# Revit family: bespoke
name_source: partatom
category: Furniture
revit_build: Autodesk Revit 2015 (Build: 20140903_1530(x64)
units: mm (PartAtom-declared; Revit-internal decimal feet)

## types (12) — shared parameters
BIMobject category = Tables
BOSUseNativeGeometries = 1
Brand url = http://www.swedese.com
Date of publishing = 3/22/2016
Design country = Sweden
Edition number = 1
IFC Classification = Furnishing Element
Manufacturer country = Sweden
Manufacturer name = Swedese
Material main = Wood
Nominal height = 720
Nominal width = 2000
OmniClass Code = 23-21 11 00
OmniClass Description = Commercial Furniture
Product Guid = 040cca99-c903-4709-9778-d5a774ea8faa
Product SKU = 27924
Product data url = https://bimobject.com
Product family = Tables
Product group = Bespoke
Product name = Bespoke
Product url = http://www.swedese.se
QR code = http://bimobject.com
Technical description = https://static-swedese.s3.amazonaws.com
UNSPSC Code = 56
Uniclass 1.4 Code = L8211
Uniclass 1.4 Description = Furniture
Weight Net (Kg) = 55

## type names (no varying parameters)
- TYPE - (Bespoke Addon Right) COLOUR - (Ash veneer)
- TYPE - (Bespoke Addon Left) COLOUR - (Ash veneer)
- TYPE - (Bespoke Addon Both) COLOUR - (Ash veneer)
- TYPE - (Bespoke 1) COLOUR - (Ash veneer)
- TYPE - (Bespoke Addon Right) COLOUR - (Oak veneer)
- TYPE - (Bespoke Addon Left) COLOUR - (Oak veneer)
- TYPE - (Bespoke Addon Both) COLOUR - (Oak veneer)
- TYPE - (Bespoke 1) COLOUR - (Oak veneer)
- TYPE - (Bespoke Addon Right) COLOUR - (White)
- TYPE - (Bespoke Addon Left) COLOUR - (White)
- TYPE - (Bespoke Addon Both) COLOUR - (White)
- TYPE - (Bespoke 1) COLOUR - (White)

## geometry (parser evidence)
native form markers: Sweep x1
no freeform markers — native parametric forms only
